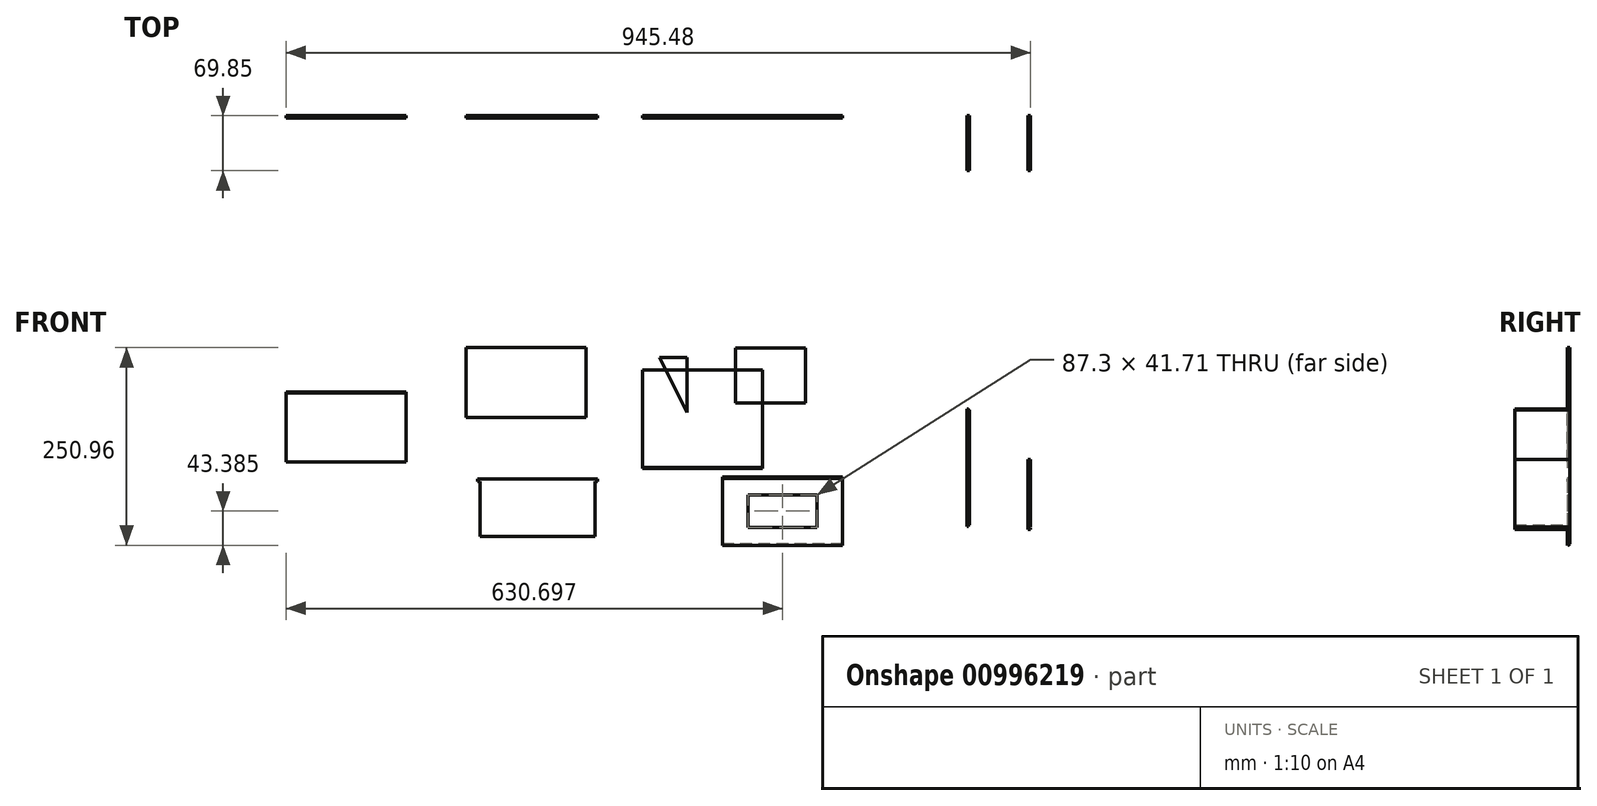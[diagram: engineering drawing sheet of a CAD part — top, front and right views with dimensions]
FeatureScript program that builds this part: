
annotation { "Feature Type Name" : "Feature", "Feature Type Description" : "" }
export const myFeature = defineFeature(function(context is Context, id is Id, definition is map)
    precondition{}
    {
        {
            var Q0;
            Q0=qCreatedBy(makeId("Front.planeOp"),FACE);
            var sketch = newSketch(context, id + "F0", { "sketchPlane" : qUnion([Q0])});
            skLineSegment(sketch, "E0.top", {"start": v(92.65, -51.57) * mm, "end": v(5.35, -51.57) * mm});
            skLineSegment(sketch, "E0.left", {"start": v(92.65, -9.86) * mm, "end": v(92.65, -51.57) * mm});
            skLineSegment(sketch, "E0.right", {"start": v(5.35, -9.86) * mm, "end": v(5.35, -51.57) * mm});
            skPoint(sketch, "E0.middle", {"position": v(49, -30.72) * mm});
            skLineSegment(sketch, "E1.bottom", {"start": v(-27.2, 12.67) * mm, "end": v(125.2, 12.67) * mm});
            skLineSegment(sketch, "E1.top", {"start": v(-27.2, -74.1) * mm, "end": v(125.2, -74.1) * mm});
            skLineSegment(sketch, "E1.left", {"start": v(-27.2, 12.67) * mm, "end": v(-27.2, -74.1) * mm});
            skLineSegment(sketch, "E1.right", {"start": v(125.2, 12.67) * mm, "end": v(125.2, -74.1) * mm});
            skLineSegment(sketch, "E2", {"start": v(5.35, -9.86) * mm, "end": v(92.65, -9.86) * mm});
            skSolve(sketch);
        }
        {
            var Q0;
            Q0=makeQuery(id+"F0.imprint","IMPRINT",FACE,{"disambiguationData":[TD([[makeQuery(id+"F0.imprint","IMPRINT",EDGE,{"derivedFrom":sQuery(id+"F0.wireOp",EDGE,"E0.top")}),1.0]])]});
            extrude(context, id + "F1", {"entities" : qUnion([Q0]), "depth" : 3.17 * mm, "offsetDistance" : 25.4 * mm});
        }
        {
            var Q0;
            Q0=qCreatedBy(makeId("Front.planeOp"),FACE);
            var sketch = newSketch(context, id + "F2", { "sketchPlane" : qUnion([Q0])});
            skLineSegment(sketch, "E3.bottom", {"start": v(23.36, 148.9) * mm, "end": v(-129.04, 148.9) * mm});
            skLineSegment(sketch, "E3.top", {"start": v(23.36, 23.48) * mm, "end": v(-129.04, 23.48) * mm});
            skLineSegment(sketch, "E3.left", {"start": v(23.36, 148.9) * mm, "end": v(23.36, 23.48) * mm});
            skLineSegment(sketch, "E3.right", {"start": v(-129.04, 148.9) * mm, "end": v(-129.04, 23.48) * mm});
            skSolve(sketch);
        }
        {
            var Q0;
            Q0=makeQuery(id+"F2.imprint","IMPRINT",FACE,{"disambiguationData":[TD([[makeQuery(id+"F2.imprint","IMPRINT",EDGE,{"derivedFrom":sQuery(id+"F2.wireOp",EDGE,"E3.bottom")}),1.0]])]});
            extrude(context, id + "F3", {"entities" : qUnion([Q0]), "depth" : 3.17 * mm, "offsetDistance" : 25.4 * mm});
        }
        {
            var Q0;
            Q0=qCreatedBy(makeId("Front.planeOp"),FACE);
            var sketch = newSketch(context, id + "F4", { "sketchPlane" : qUnion([Q0])});
            skLineSegment(sketch, "E4.bottom", {"start": v(-189.46, -62.68) * mm, "end": v(-335.51, -62.68) * mm});
            skLineSegment(sketch, "E4.top", {"start": v(-186.29, 10.35) * mm, "end": v(-338.69, 10.35) * mm});
            skLineSegment(sketch, "E4.left", {"start": v(-186.29, 7.17) * mm, "end": v(-186.29, 10.35) * mm});
            skLineSegment(sketch, "E4.right", {"start": v(-338.69, 7.17) * mm, "end": v(-338.69, 10.35) * mm});
            skLineSegment(sketch, "E5", {"start": v(-338.69, 10.35) * mm, "end": v(-338.69, 7.17) * mm});
            skLineSegment(sketch, "E6", {"start": v(-338.69, 7.17) * mm, "end": v(-335.51, 7.17) * mm});
            skLineSegment(sketch, "E7", {"start": v(-335.51, 7.17) * mm, "end": v(-335.51, -62.68) * mm});
            skLineSegment(sketch, "E8", {"start": v(-186.29, 10.35) * mm, "end": v(-186.29, 7.17) * mm});
            skLineSegment(sketch, "E9", {"start": v(-186.29, 7.17) * mm, "end": v(-189.46, 7.17) * mm});
            skLineSegment(sketch, "E10", {"start": v(-189.46, 7.17) * mm, "end": v(-189.46, -62.68) * mm});
            skSolve(sketch);
        }
        {
            var Q0;
            Q0=makeQuery(id+"F4.imprint","IMPRINT",FACE,{"disambiguationData":[TD([[makeQuery(id+"F4.imprint","IMPRINT",EDGE,{"derivedFrom":sQuery(id+"F4.wireOp",EDGE,"E4.bottom")}),-1.0]])]});
            extrude(context, id + "F5", {"entities" : qUnion([Q0]), "depth" : 3.17 * mm, "offsetDistance" : 25.4 * mm});
        }
        {
            var Q0;
            Q0=qCreatedBy(makeId("Front.planeOp"),FACE);
            var sketch = newSketch(context, id + "F6", { "sketchPlane" : qUnion([Q0])});
            skLineSegment(sketch, "E11.bottom", {"start": v(-200.97, 176.86) * mm, "end": v(-353.37, 176.86) * mm});
            skLineSegment(sketch, "E11.top", {"start": v(-200.97, 87.96) * mm, "end": v(-353.37, 87.96) * mm});
            skLineSegment(sketch, "E11.left", {"start": v(-200.97, 176.86) * mm, "end": v(-200.97, 87.96) * mm});
            skLineSegment(sketch, "E11.right", {"start": v(-353.37, 176.86) * mm, "end": v(-353.37, 87.96) * mm});
            skSolve(sketch);
        }
        {
            var Q0;
            Q0=makeQuery(id+"F6.imprint","IMPRINT",FACE,{"disambiguationData":[TD([[makeQuery(id+"F6.imprint","IMPRINT",EDGE,{"derivedFrom":sQuery(id+"F6.wireOp",EDGE,"E11.bottom")}),1.0]])]});
            extrude(context, id + "F7", {"entities" : qUnion([Q0]), "depth" : 3.17 * mm, "offsetDistance" : 25.4 * mm});
        }
        {
            var Q0;
            Q0=qCreatedBy(makeId("Front.planeOp"),FACE);
            var sketch = newSketch(context, id + "F8", { "sketchPlane" : qUnion([Q0])});
            skLineSegment(sketch, "E12", {"start": v(-72.35, 94.85) * mm, "end": v(-72.35, 164.7) * mm});
            skLineSegment(sketch, "E13", {"start": v(-72.35, 164.7) * mm, "end": v(-107.28, 164.7) * mm});
            skLineSegment(sketch, "E14", {"start": v(-107.28, 164.7) * mm, "end": v(-72.35, 94.85) * mm});
            skSolve(sketch);
        }
        {
            var Q0;
            Q0=makeQuery(id+"F8.imprint","IMPRINT",FACE,{"disambiguationData":[TD([[makeQuery(id+"F8.imprint","IMPRINT",EDGE,{"derivedFrom":sQuery(id+"F8.wireOp",EDGE,"E12")}),1.0]])]});
            extrude(context, id + "F9", {"entities" : qUnion([Q0]), "depth" : 3.17 * mm, "offsetDistance" : 25.4 * mm});
        }
        {
            var Q0;
            Q0=qCreatedBy(makeId("Front.planeOp"),FACE);
            var sketch = newSketch(context, id + "F10", { "sketchPlane" : qUnion([Q0])});
            skLineSegment(sketch, "E15.top", {"start": v(-10.59, 106.8) * mm, "end": v(78.31, 106.8) * mm});
            skLineSegment(sketch, "E15.left", {"start": v(-10.59, 176.66) * mm, "end": v(-10.59, 106.8) * mm});
            skLineSegment(sketch, "E15.right", {"start": v(78.31, 176.66) * mm, "end": v(78.31, 106.8) * mm});
            skLineSegment(sketch, "E16", {"start": v(-10.59, 176.66) * mm, "end": v(78.31, 176.66) * mm});
            skSolve(sketch);
        }
        {
            var Q0;
            {var subQ0=sQuery(id+"F10.wireOp",EDGE,"E15.left");Q0=makeQuery(id+"F10.imprint","IMPRINT",FACE,{"disambiguationData":[TD([[makeQuery(id+"F10.imprint","IMPRINT",EDGE,{"derivedFrom":subQ0}),1.0]])]});}
            extrude(context, id + "F11", {"entities" : qUnion([Q0]), "depth" : 3.17 * mm, "offsetDistance" : 25.4 * mm});
        }
        {
            var Q0;
            Q0=makeQuery(id+"F1.opExtrude","CAP_EDGE",EDGE,{"disambiguationData":[OSD([sQuery(id+"F0.wireOp",EDGE,"E1.top")])],"isStart":true});
            chamfer(context, id + "F12", {"entities" : qUnion([Q0]), "chamferType" : ChamferType.OFFSET_ANGLE, "width" : 3.17 * mm, "oppositeDirection" : false, "angle" : 25.56 * degree, "tangentPropagation" : true});
        }
        {
            var Q0;
            Q0=makeQuery(id+"F1.opExtrude","CAP_EDGE",EDGE,{"disambiguationData":[OSD([sQuery(id+"F0.wireOp",EDGE,"E1.bottom")])],"isStart":false});
            chamfer(context, id + "F13", {"entities" : qUnion([Q0]), "chamferType" : ChamferType.OFFSET_ANGLE, "width" : 3.17 * mm, "oppositeDirection" : false, "angle" : 26.56 * degree, "tangentPropagation" : true});
        }
        {
            var Q0;
            Q0=qCreatedBy(makeId("Front.planeOp"),FACE);
            var sketch = newSketch(context, id + "F14", { "sketchPlane" : qUnion([Q0])});
            skLineSegment(sketch, "E17.bottom", {"start": v(-581.7, 32) * mm, "end": v(-429.3, 32) * mm});
            skLineSegment(sketch, "E17.top", {"start": v(-581.7, 120.9) * mm, "end": v(-429.3, 120.9) * mm});
            skLineSegment(sketch, "E17.left", {"start": v(-581.7, 32) * mm, "end": v(-581.7, 120.9) * mm});
            skLineSegment(sketch, "E17.right", {"start": v(-429.3, 32) * mm, "end": v(-429.3, 120.9) * mm});
            skPoint(sketch, "E17.middle", {"position": v(-505.5, 76.46) * mm});
            skSolve(sketch);
        }
        {
            var Q0;
            Q0=makeQuery(id+"F14.imprint","IMPRINT",FACE,{"disambiguationData":[TD([[makeQuery(id+"F14.imprint","IMPRINT",EDGE,{"derivedFrom":sQuery(id+"F14.wireOp",EDGE,"E17.bottom")}),1.0]])]});
            extrude(context, id + "F15", {"entities" : qUnion([Q0]), "depth" : 3.17 * mm, "offsetDistance" : 25.4 * mm});
        }
        {
            var Q0;
            Q0=makeQuery(id+"F15.opExtrude","CAP_EDGE",EDGE,{"disambiguationData":[OSD([sQuery(id+"F14.wireOp",EDGE,"E17.top")])],"isStart":false});
            chamfer(context, id + "F16", {"entities" : qUnion([Q0]), "chamferType" : ChamferType.OFFSET_ANGLE, "width" : 3.17 * mm, "oppositeDirection" : false, "angle" : 26.56 * degree, "tangentPropagation" : true});
        }
        {
            var Q0;
            Q0=makeQuery(id+"F3.opExtrude","CAP_EDGE",EDGE,{"disambiguationData":[OSD([sQuery(id+"F2.wireOp",EDGE,"E3.top")])],"isStart":false});
            chamfer(context, id + "F17", {"entities" : qUnion([Q0]), "chamferType" : ChamferType.OFFSET_ANGLE, "width" : 3.17 * mm, "oppositeDirection" : false, "angle" : 26.56 * degree, "tangentPropagation" : true});
        }
        {
            var Q0;
            Q0=qCreatedBy(makeId("Front.planeOp"),FACE);
            var sketch = newSketch(context, id + "F18", { "sketchPlane" : qUnion([Q0])});
            skLineSegment(sketch, "E18", {"start": v(360.6, 35.07) * mm, "end": v(360.6, -53.83) * mm});
            skLineSegment(sketch, "E19", {"start": v(360.6, -53.83) * mm, "end": v(363.78, -53.83) * mm});
            skLineSegment(sketch, "E20", {"start": v(363.78, -53.83) * mm, "end": v(363.78, -52.24) * mm});
            skLineSegment(sketch, "E21", {"start": v(363.78, -50.65) * mm, "end": v(363.78, 35.07) * mm});
            skLineSegment(sketch, "E22", {"start": v(360.6, 35.07) * mm, "end": v(363.78, 35.07) * mm});
            skLineSegment(sketch, "E23", {"start": v(363.78, -52.24) * mm, "end": v(362.2, -52.24) * mm});
            skLineSegment(sketch, "E24", {"start": v(362.2, -52.24) * mm, "end": v(362.2, -50.65) * mm});
            skLineSegment(sketch, "E25", {"start": v(363.78, -50.65) * mm, "end": v(362.2, -50.65) * mm});
            skSolve(sketch);
        }
        {
            var Q0;
            Q0=makeQuery(id+"F18.imprint","IMPRINT",FACE,{"disambiguationData":[TD([[makeQuery(id+"F18.imprint","IMPRINT",EDGE,{"derivedFrom":sQuery(id+"F18.wireOp",EDGE,"E18")}),1.0]])]});
            extrude(context, id + "F19", {"entities" : qUnion([Q0]), "depth" : 69.85 * mm, "offsetDistance" : 25.4 * mm});
        }
        {
            var Q0;
            Q0=qCreatedBy(makeId("Front.planeOp"),FACE);
            var sketch = newSketch(context, id + "F20", { "sketchPlane" : qUnion([Q0])});
            skLineSegment(sketch, "E26", {"start": v(285, 99.25) * mm, "end": v(283.41, 99.25) * mm});
            skLineSegment(sketch, "E27", {"start": v(286.59, 97.66) * mm, "end": v(286.59, -48.39) * mm});
            skLineSegment(sketch, "E28", {"start": v(285, -49.97) * mm, "end": v(283.41, -49.97) * mm});
            skLineSegment(sketch, "E29", {"start": v(283.41, 99.25) * mm, "end": v(283.41, -49.97) * mm});
            skLineSegment(sketch, "E30", {"start": v(286.59, -48.39) * mm, "end": v(285, -48.39) * mm});
            skLineSegment(sketch, "E31", {"start": v(285, -48.39) * mm, "end": v(285, -49.97) * mm});
            skLineSegment(sketch, "E32", {"start": v(286.59, 97.66) * mm, "end": v(285, 97.66) * mm});
            skLineSegment(sketch, "E33", {"start": v(285, 97.66) * mm, "end": v(285, 99.25) * mm});
            skLineSegment(sketch, "E34", {"start": v(283.41, 99.25) * mm, "end": v(285, 99.25) * mm});
            skSolve(sketch);
        }
        {
            var Q0;
            Q0=makeQuery(id+"F20.imprint","IMPRINT",FACE,{"disambiguationData":[TD([[makeQuery(id+"F20.imprint","IMPRINT",EDGE,{"derivedFrom":sQuery(id+"F20.wireOp",EDGE,"E27")}),-1.0]])]});
            extrude(context, id + "F21", {"entities" : qUnion([Q0]), "depth" : 69.85 * mm, "offsetDistance" : 25.4 * mm});
        }
    });
